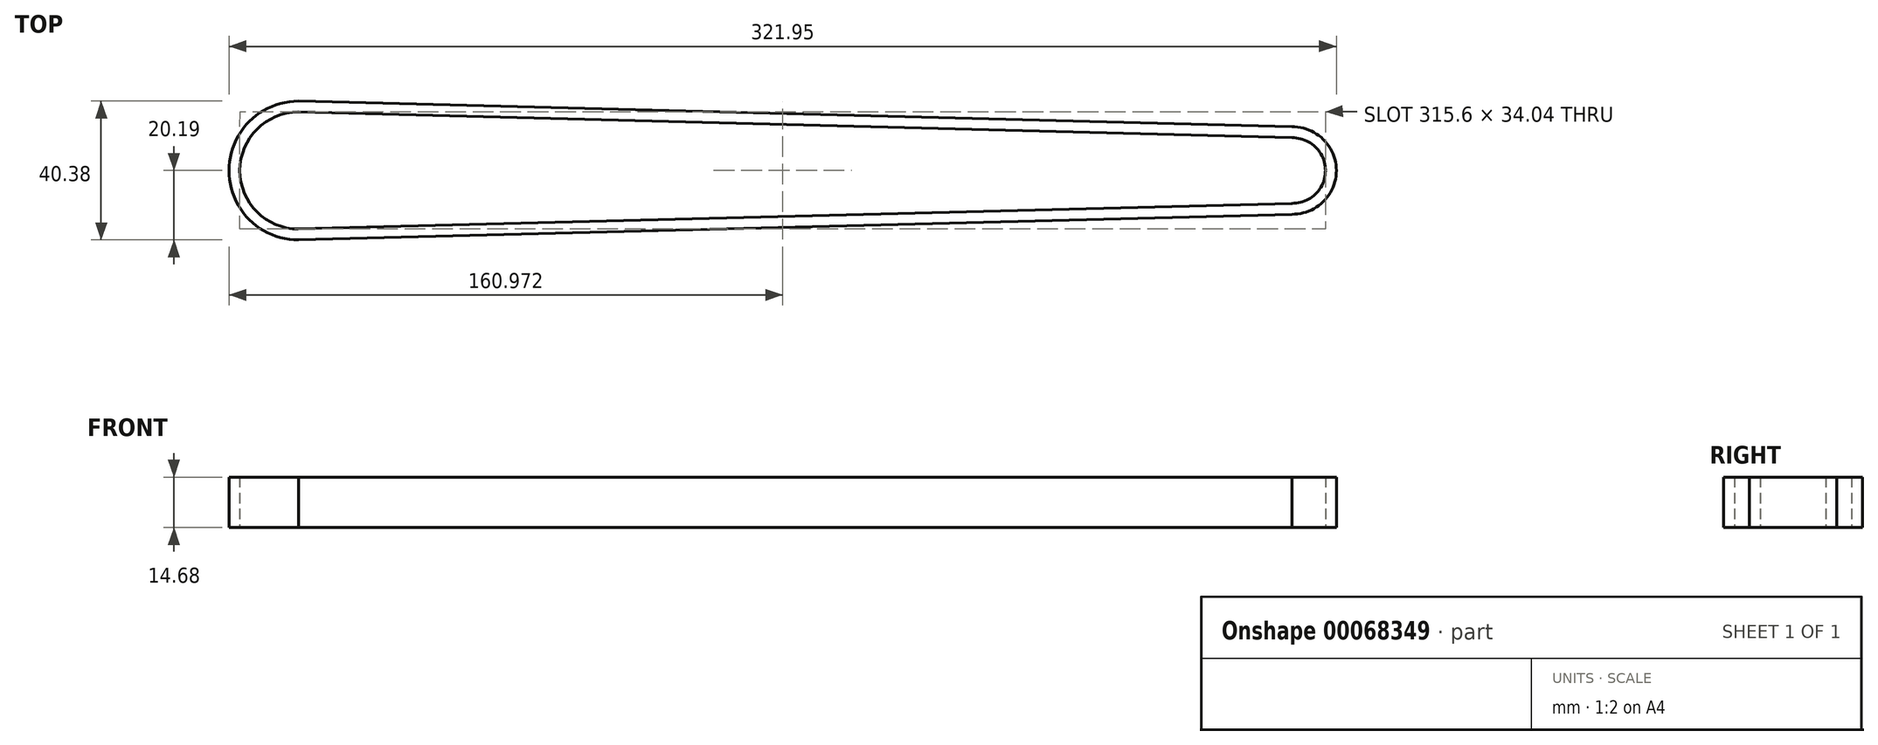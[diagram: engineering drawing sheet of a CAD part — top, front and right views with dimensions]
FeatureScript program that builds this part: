
annotation { "Feature Type Name" : "Feature", "Feature Type Description" : "" }
export const myFeature = defineFeature(function(context is Context, id is Id, definition is map)
    precondition{}
    {
        {
            var Q0;
            Q0=qCreatedBy(makeId("Top.planeOp"),FACE);
            var sketch = newSketch(context, id + "F0", { "sketchPlane" : qUnion([Q0])});
            skLineSegment(sketch, "E0", {"start": v(-0.24, -9.53) * mm, "end": v(-289.05, -17.02) * mm});
            skLineSegment(sketch, "E1", {"start": v(-289.05, 17.02) * mm, "end": v(-0.24, 9.53) * mm});
            skArc(sketch, "E2", {"start": v(-289.05, 17.02) * mm, "mid": v(-306.07, 0) * mm, "end": v(-289.05, -17.02) * mm});
            skArc(sketch, "E3", {"start": v(-0.24, -9.53) * mm, "mid": v(9.53, 0) * mm, "end": v(-0.24, 9.53) * mm});
            skLineSegment(sketch, "E4.0", {"start": v(-289, 20.2) * mm, "end": v(-0.24, 12.7) * mm});
            skArc(sketch, "E4.1", {"start": v(-289, 20.2) * mm, "mid": v(-309.25, 0) * mm, "end": v(-289, -20.2) * mm});
            skLineSegment(sketch, "E4.2", {"start": v(-0.24, -12.7) * mm, "end": v(-289, -20.2) * mm});
            skArc(sketch, "E4.3", {"start": v(-0.24, -12.7) * mm, "mid": v(12.7, 0) * mm, "end": v(-0.24, 12.7) * mm});
            skSolve(sketch);
        }
        {
            var Q0;
            Q0=makeQuery(id+"F0.imprint","IMPRINT",FACE,{"disambiguationData":[TD([[makeQuery(id+"F0.imprint","IMPRINT",EDGE,{"derivedFrom":sQuery(id+"F0.wireOp",EDGE,"E0")}),1.0]])]});
            extrude(context, id + "F1", {"entities" : qUnion([Q0]), "depth" : 14.68 * mm});
        }
    });
